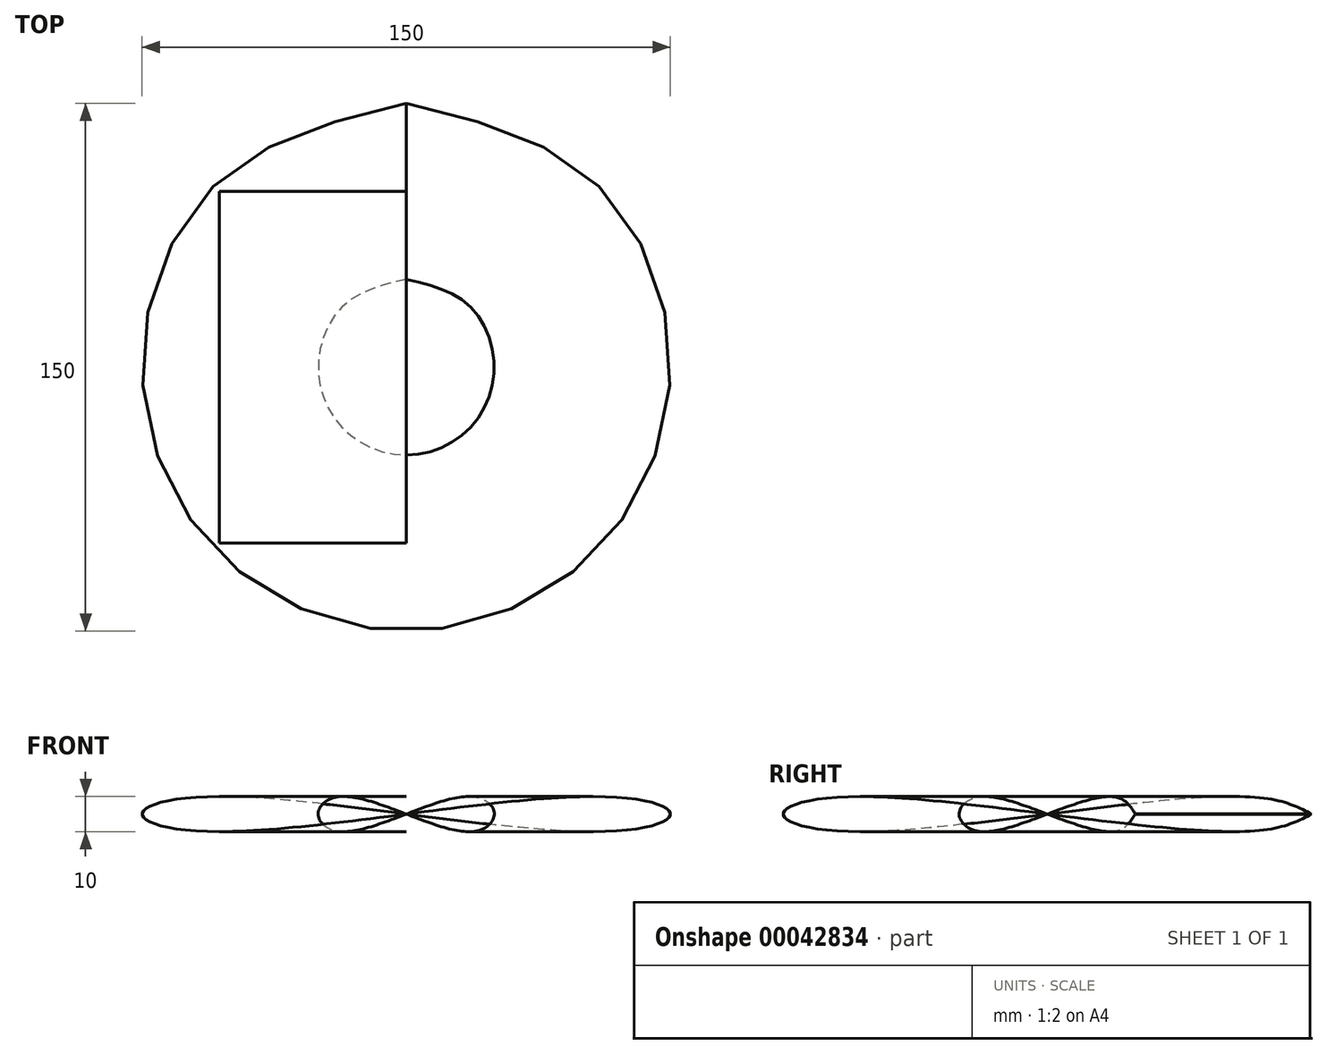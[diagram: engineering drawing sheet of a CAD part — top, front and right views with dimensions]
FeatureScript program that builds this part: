
annotation { "Feature Type Name" : "Feature", "Feature Type Description" : "" }
export const myFeature = defineFeature(function(context is Context, id is Id, definition is map)
    precondition{}
    {
        {
            var Q0;
            Q0=qCreatedBy(makeId("Top.planeOp"),FACE);
            var sketch = newSketch(context, id + "F0", { "sketchPlane" : qUnion([Q0])});
            skCircle(sketch, "E0", {"center": v(0, 0) * mm, "radius": 25 * mm});
            skCircle(sketch, "E1", {"center": v(0, 0) * mm, "radius": 75 * mm});
            skLineSegment(sketch, "E2", {"start": v(0, 25) * mm, "end": v(0, 75) * mm});
            skCircle(sketch, "E3", {"center": v(0, 0) * mm, "radius": 37.5 * mm});
            skCircle(sketch, "E4", {"center": v(0, 0) * mm, "radius": 62.5 * mm});
            skLineSegment(sketch, "E5.1.0", {"start": v(-17.68, 17.68) * mm, "end": v(-53.03, 53.03) * mm});
            skLineSegment(sketch, "E5.2.0", {"start": v(-25, 0) * mm, "end": v(-75, 0) * mm});
            skLineSegment(sketch, "E5.3.0", {"start": v(-17.68, -17.68) * mm, "end": v(-53.03, -53.03) * mm});
            skLineSegment(sketch, "E5.4.0", {"start": v(0, -25) * mm, "end": v(0, -75) * mm});
            skLineSegment(sketch, "E5.5.0", {"start": v(17.68, -17.68) * mm, "end": v(53.03, -53.03) * mm});
            skLineSegment(sketch, "E5.6.0", {"start": v(25, 0) * mm, "end": v(75, 0) * mm});
            skLineSegment(sketch, "E5.7.0", {"start": v(17.68, 17.68) * mm, "end": v(53.03, 53.03) * mm});
            skLineSegment(sketch, "E5.anchor1", {"start": v(0, 0) * mm, "end": v(0, 25) * mm, "construction": true});
            skLineSegment(sketch, "E5.anchor2", {"start": v(0, 0) * mm, "end": v(0, 25) * mm, "construction": true});
            skSolve(sketch);
        }
        {
            var Q0;
            Q0=qCreatedBy(makeId("Top.planeOp"),FACE);
            cPlane(context, id + "F1", {"entities" : qUnion([Q0]), "cplaneType" : CPlaneType.OFFSET, "offset" : 0.01 * mm, "width" : 150 * mm, "height" : 150 * mm});
        }
        {
            var Q0;
            Q0=qCreatedBy(id+"F1.planeOp",FACE);
            var sketch = newSketch(context, id + "F2", { "sketchPlane" : qUnion([Q0])});
            skLineSegment(sketch, "E6.0", {"start": v(0, 25) * mm, "end": v(0, 75) * mm});
            skSolve(sketch);
        }
        {
            var Q0;
            Q0=qCreatedBy(makeId("Front.planeOp"),FACE);
            var sketch = newSketch(context, id + "F3", { "sketchPlane" : qUnion([Q0])});
            skLineSegment(sketch, "E7", {"start": v(-53.03, -5) * mm, "end": v(0, -5) * mm});
            skLineSegment(sketch, "E8", {"start": v(-53.03, 5) * mm, "end": v(0, 5) * mm});
            skLineSegment(sketch, "E9", {"start": v(5.43, 0) * mm, "end": v(42.33, 0) * mm, "construction": true});
            skSolve(sketch);
        }
        {
            var Q0;
            Q0=sQuery(id+"F3.wireOp",EDGE,"E8");
            var Q1;
            Q1=sQuery(id+"F3.wireOp",EDGE,"E7");
            extrude(context, id + "F4", {"bodyType" : ToolBodyType.SURFACE, "surfaceEntities" : qUnion([Q0, Q1]), "endBound" : BoundingType.SYMMETRIC, "depth" : 100 * mm});
        }
        {
            var Q0;
            Q0=makeQuery(id+"F4.opExtrude","SWEPT_FACE",FACE,{"disambiguationData":[OSD([sQuery(id+"F3.wireOp",EDGE,"E8")])]});
            var sketch = newSketch(context, id + "F5", { "sketchPlane" : qUnion([Q0])});
            skLineSegment(sketch, "E10.0", {"start": v(-17.68, -17.68) * mm, "end": v(-53.03, -53.03) * mm});
            skLineSegment(sketch, "E10.1", {"start": v(17.68, 17.68) * mm, "end": v(53.03, 53.03) * mm});
            skSolve(sketch);
        }
        {
            var Q0;
            Q0=makeQuery(id+"F4.opExtrude","SWEPT_FACE",FACE,{"disambiguationData":[OSD([sQuery(id+"F3.wireOp",EDGE,"E7")])]});
            var sketch = newSketch(context, id + "F6", { "sketchPlane" : qUnion([Q0])});
            skLineSegment(sketch, "E11.0", {"start": v(-17.68, 17.68) * mm, "end": v(-53.03, 53.03) * mm});
            skLineSegment(sketch, "E11.1", {"start": v(17.68, -17.68) * mm, "end": v(53.03, -53.03) * mm});
            skSolve(sketch);
        }
        {
            var Q0;
            Q0=sQuery(id+"F0.wireOp",EDGE,"E2");
            var Q1;
            Q1=sQuery(id+"F5.wireOp",EDGE,"E10.0");
            var Q2;
            Q2=sQuery(id+"F0.wireOp",EDGE,"E5.2.0");
            var Q3;
            Q3=sQuery(id+"F6.wireOp",EDGE,"E11.0");
            var Q4;
            Q4=sQuery(id+"F0.wireOp",EDGE,"E5.4.0");
            var Q5;
            Q5=sQuery(id+"F5.wireOp",EDGE,"E10.1");
            var Q6;
            Q6=sQuery(id+"F0.wireOp",EDGE,"E5.6.0");
            var Q7;
            Q7=sQuery(id+"F6.wireOp",EDGE,"E11.1");
            var Q8;
            Q8=sQuery(id+"F2.wireOp",EDGE,"E6.0");
            loft(context, id + "F7", {"bodyType" : ToolBodyType.SURFACE, "wireProfilesArray" : [{ "wireProfileEntities" : qUnion([Q0]) }, { "wireProfileEntities" : qUnion([Q1]) }, { "wireProfileEntities" : qUnion([Q2]) }, { "wireProfileEntities" : qUnion([Q3]) }, { "wireProfileEntities" : qUnion([Q4]) }, { "wireProfileEntities" : qUnion([Q5]) }, { "wireProfileEntities" : qUnion([Q6]) }, { "wireProfileEntities" : qUnion([Q7]) }, { "wireProfileEntities" : qUnion([Q8]) }]});
        }
    });
